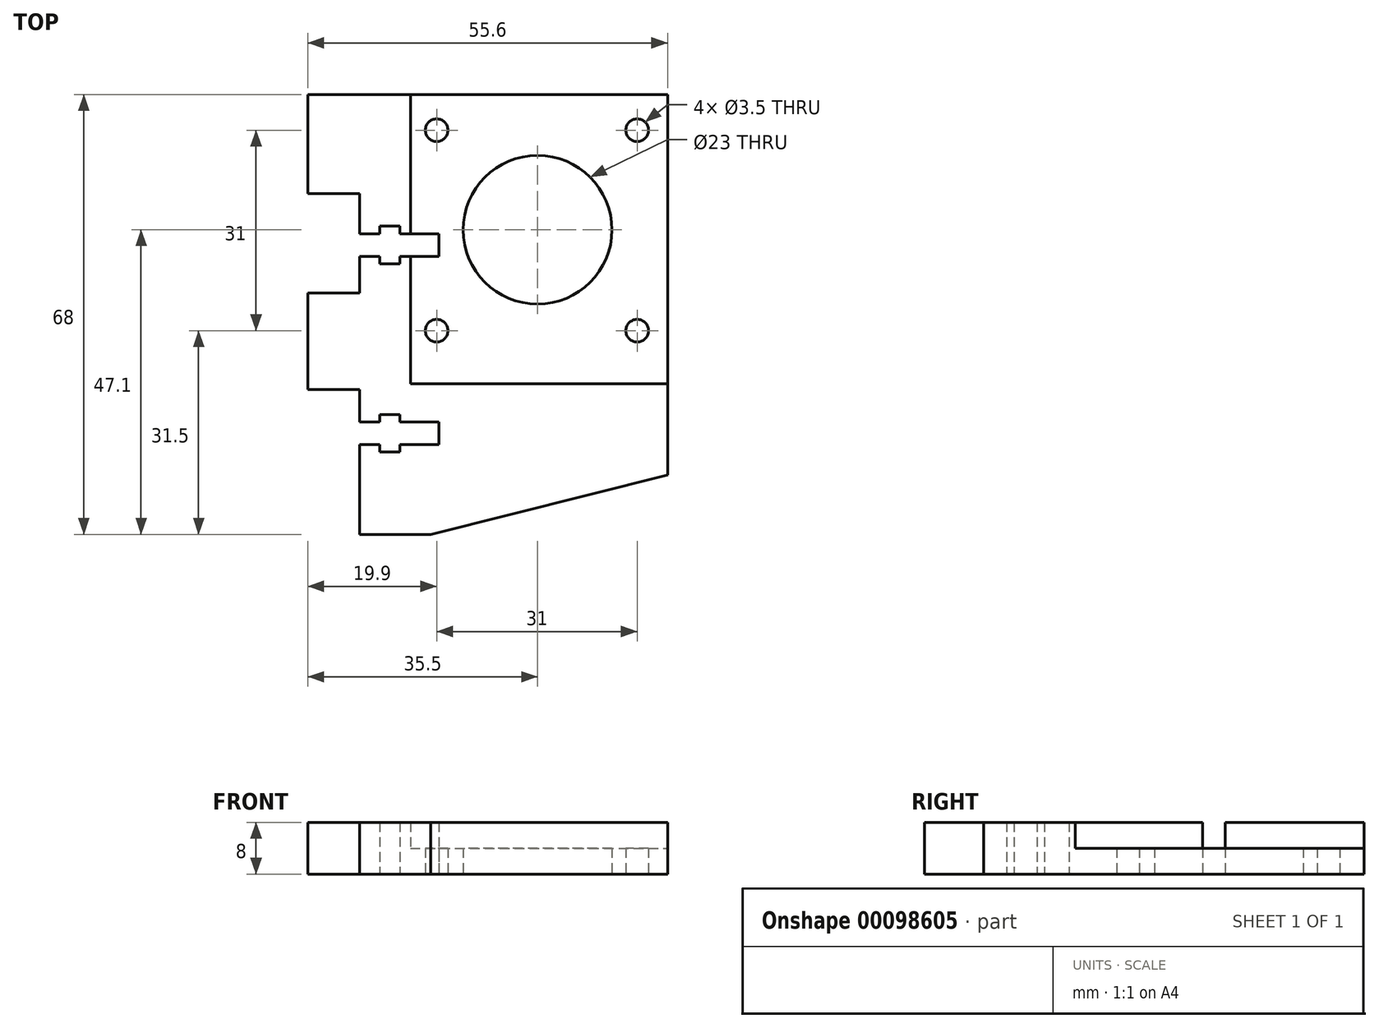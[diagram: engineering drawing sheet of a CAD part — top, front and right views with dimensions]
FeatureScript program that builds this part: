
annotation { "Feature Type Name" : "Feature", "Feature Type Description" : "" }
export const myFeature = defineFeature(function(context is Context, id is Id, definition is map)
    precondition{}
    {
        {
            var Q0;
            Q0=qCreatedBy(makeId("Top.planeOp"),FACE);
            var sketch = newSketch(context, id + "F0", { "sketchPlane" : qUnion([Q0])});
            skCircle(sketch, "E0", {"center": v(0, 0) * mm, "radius": 11.5 * mm});
            skLineSegment(sketch, "E1", {"start": v(0, 11.5) * mm, "end": v(0, 20.9) * mm, "construction": true});
            skLineSegment(sketch, "E2", {"start": v(11.5, 0) * mm, "end": v(20.1, 0) * mm, "construction": true});
            skLineSegment(sketch, "E3", {"start": v(0, 20.9) * mm, "end": v(58.5, 20.9) * mm, "construction": true});
            skLineSegment(sketch, "E4", {"start": v(20.1, 0) * mm, "end": v(20.1, 20.9) * mm});
            skLineSegment(sketch, "E5", {"start": v(-11.5, 0) * mm, "end": v(-27.86, 0) * mm, "construction": true});
            skLineSegment(sketch, "E6", {"start": v(20.1, 0) * mm, "end": v(20.1, -40.2) * mm, "construction": true});
            skLineSegment(sketch, "E7", {"start": v(20.1, -37.9) * mm, "end": v(-35.5, -37.9) * mm, "construction": true});
            skLineSegment(sketch, "E8", {"start": v(0, 20.9) * mm, "end": v(-51.46, 20.9) * mm, "construction": true});
            skLineSegment(sketch, "E9", {"start": v(-35.5, 20.9) * mm, "end": v(-35.5, 5.6) * mm});
            skLineSegment(sketch, "E10", {"start": v(-27.5, -47.1) * mm, "end": v(-16.5, -47.1) * mm});
            skLineSegment(sketch, "E11", {"start": v(20.1, 20.9) * mm, "end": v(20.1, -37.9) * mm});
            skLineSegment(sketch, "E12", {"start": v(-16.5, -47.1) * mm, "end": v(20.1, -37.9) * mm});
            skLineSegment(sketch, "E13.0", {"start": v(-27.5, 5.6) * mm, "end": v(-27.5, -0.6) * mm});
            skLineSegment(sketch, "E14", {"start": v(-32.15, -47.1) * mm, "end": v(-32.15, -24.7) * mm, "construction": true});
            skLineSegment(sketch, "E15", {"start": v(-32.15, -24.7) * mm, "end": v(-27.5, -24.7) * mm});
            skLineSegment(sketch, "E16", {"start": v(-27.5, -24.7) * mm, "end": v(-35.5, -24.7) * mm});
            skLineSegment(sketch, "E17", {"start": v(-32.15, -24.7) * mm, "end": v(-32.15, -9.8) * mm, "construction": true});
            skLineSegment(sketch, "E18", {"start": v(-27.5, -9.8) * mm, "end": v(-35.5, -9.8) * mm});
            skLineSegment(sketch, "E19", {"start": v(-32.15, -9.8) * mm, "end": v(-32.15, 5.6) * mm, "construction": true});
            skLineSegment(sketch, "E20", {"start": v(-32.15, 5.6) * mm, "end": v(-27.5, 5.6) * mm});
            skLineSegment(sketch, "E21", {"start": v(-27.5, 5.6) * mm, "end": v(-35.5, 5.6) * mm});
            skLineSegment(sketch, "E22.trimOffspring", {"start": v(-35.5, -9.8) * mm, "end": v(-35.5, -24.7) * mm});
            skLineSegment(sketch, "E23", {"start": v(-35.5, 20.9) * mm, "end": v(20.1, 20.9) * mm});
            skLineSegment(sketch, "E24.trimOffspring", {"start": v(-27.5, -24.7) * mm, "end": v(-27.5, -29.7) * mm});
            skLineSegment(sketch, "E25.0", {"start": v(-35.5, 15.4) * mm, "end": v(20.1, 15.4) * mm, "construction": true});
            skLineSegment(sketch, "E26.0", {"start": v(15.4, 20.9) * mm, "end": v(15.4, -37.9) * mm, "construction": true});
            skCircle(sketch, "E27", {"center": v(15.4, 15.4) * mm, "radius": 1.75 * mm});
            skLineSegment(sketch, "E28", {"start": v(15.4, 15.4) * mm, "end": v(-15.6, 15.4) * mm, "construction": true});
            skCircle(sketch, "E29", {"center": v(-15.6, 15.4) * mm, "radius": 1.75 * mm});
            skLineSegment(sketch, "E30", {"start": v(-15.6, 15.4) * mm, "end": v(-15.6, -15.6) * mm, "construction": true});
            skCircle(sketch, "E31", {"center": v(-15.6, -15.6) * mm, "radius": 1.75 * mm});
            skLineSegment(sketch, "E32", {"start": v(-15.6, -15.6) * mm, "end": v(15.4, -15.6) * mm, "construction": true});
            skCircle(sketch, "E33", {"center": v(15.4, -15.6) * mm, "radius": 1.75 * mm});
            skLineSegment(sketch, "E34", {"start": v(-24.4, 20.9) * mm, "end": v(-24.4, -0.6) * mm, "construction": true});
            skLineSegment(sketch, "E35.bottom", {"start": v(-27.5, -0.6) * mm, "end": v(-24.39, -0.6) * mm});
            skLineSegment(sketch, "E35.top", {"start": v(-27.5, -4.1) * mm, "end": v(-24.39, -4.1) * mm});
            skLineSegment(sketch, "E35.right", {"start": v(-15.26, -0.6) * mm, "end": v(-15.26, -4.1) * mm});
            skLineSegment(sketch, "E36.trimOffspring", {"start": v(-27.5, -4.1) * mm, "end": v(-27.5, -9.8) * mm});
            skLineSegment(sketch, "E37", {"start": v(-24.39, -4.1) * mm, "end": v(-24.39, -29.7) * mm, "construction": true});
            skLineSegment(sketch, "E38.bottom", {"start": v(-27.5, -29.7) * mm, "end": v(-24.39, -29.7) * mm});
            skLineSegment(sketch, "E38.top", {"start": v(-27.5, -33.2) * mm, "end": v(-24.39, -33.2) * mm});
            skLineSegment(sketch, "E38.right", {"start": v(-15.26, -29.7) * mm, "end": v(-15.26, -33.2) * mm});
            skLineSegment(sketch, "E39.trimOffspring", {"start": v(-27.5, -33.2) * mm, "end": v(-27.5, -47.1) * mm});
            skLineSegment(sketch, "E40.0", {"start": v(-23.1, 5.6) * mm, "end": v(-23.1, -0.6) * mm, "construction": true});
            skLineSegment(sketch, "E41.bottom", {"start": v(-24.4, -0.6) * mm, "end": v(-23.1, -0.6) * mm, "construction": true});
            skLineSegment(sketch, "E41.top", {"start": v(-24.4, -4.1) * mm, "end": v(-21.3, -4.1) * mm, "construction": true});
            skLineSegment(sketch, "E41.left", {"start": v(-24.4, -0.6) * mm, "end": v(-24.4, -4.1) * mm, "construction": true});
            skLineSegment(sketch, "E41.right", {"start": v(-21.3, -0.6) * mm, "end": v(-21.3, -4.1) * mm, "construction": true});
            skLineSegment(sketch, "E42.0", {"start": v(-27.5, -5.25) * mm, "end": v(-15.26, -5.25) * mm, "construction": true});
            skLineSegment(sketch, "E43.bottom", {"start": v(-24.39, -5.25) * mm, "end": v(-21.29, -5.25) * mm, "construction": true});
            skLineSegment(sketch, "E43.top", {"start": v(-24.39, 0.55) * mm, "end": v(-21.29, 0.55) * mm, "construction": true});
            skLineSegment(sketch, "E43.left", {"start": v(-24.39, -5.25) * mm, "end": v(-24.39, 0.55) * mm, "construction": true});
            skLineSegment(sketch, "E43.right", {"start": v(-21.29, -5.25) * mm, "end": v(-21.29, 0.55) * mm, "construction": true});
            skLineSegment(sketch, "E44.bottom", {"start": v(-24.39, 0.55) * mm, "end": v(-21.29, 0.55) * mm});
            skLineSegment(sketch, "E44.top", {"start": v(-24.39, -5.25) * mm, "end": v(-21.29, -5.25) * mm});
            skLineSegment(sketch, "E44.left", {"start": v(-24.39, 0.55) * mm, "end": v(-24.39, -0.6) * mm});
            skLineSegment(sketch, "E44.right", {"start": v(-21.29, 0.55) * mm, "end": v(-21.29, -0.6) * mm});
            skLineSegment(sketch, "E45.trimOffspring", {"start": v(-21.3, -0.6) * mm, "end": v(-15.26, -0.6) * mm});
            skLineSegment(sketch, "E46.trimOffspring", {"start": v(-24.39, -4.1) * mm, "end": v(-24.39, -5.25) * mm});
            skLineSegment(sketch, "E47.trimOffspring", {"start": v(-21.29, -4.1) * mm, "end": v(-21.29, -5.25) * mm});
            skLineSegment(sketch, "E48.trimOffspring", {"start": v(-21.3, -4.1) * mm, "end": v(-15.26, -4.1) * mm});
            skLineSegment(sketch, "E49.0", {"start": v(-27.5, -34.35) * mm, "end": v(-15.26, -34.35) * mm, "construction": true});
            skLineSegment(sketch, "E50.bottom", {"start": v(-24.39, -34.35) * mm, "end": v(-21.29, -34.35) * mm, "construction": true});
            skLineSegment(sketch, "E50.top", {"start": v(-24.39, -28.55) * mm, "end": v(-21.29, -28.55) * mm, "construction": true});
            skLineSegment(sketch, "E50.left", {"start": v(-24.39, -34.35) * mm, "end": v(-24.39, -28.55) * mm, "construction": true});
            skLineSegment(sketch, "E50.right", {"start": v(-21.29, -34.35) * mm, "end": v(-21.29, -28.55) * mm, "construction": true});
            skLineSegment(sketch, "E51.bottom", {"start": v(-24.39, -28.55) * mm, "end": v(-21.29, -28.55) * mm});
            skLineSegment(sketch, "E51.top", {"start": v(-24.39, -34.35) * mm, "end": v(-21.29, -34.35) * mm});
            skLineSegment(sketch, "E51.left", {"start": v(-24.39, -28.55) * mm, "end": v(-24.39, -29.7) * mm});
            skLineSegment(sketch, "E51.right", {"start": v(-21.29, -28.55) * mm, "end": v(-21.29, -29.7) * mm});
            skLineSegment(sketch, "E52.trimOffspring", {"start": v(-21.29, -29.7) * mm, "end": v(-15.26, -29.7) * mm});
            skLineSegment(sketch, "E53.trimOffspring", {"start": v(-21.29, -33.2) * mm, "end": v(-15.26, -33.2) * mm});
            skLineSegment(sketch, "E54.trimOffspring", {"start": v(-21.29, -33.2) * mm, "end": v(-21.29, -34.35) * mm});
            skLineSegment(sketch, "E55.trimOffspring", {"start": v(-24.39, -33.2) * mm, "end": v(-24.39, -34.35) * mm});
            skSolve(sketch);
        }
        {
            var Q0;
            Q0=makeQuery(id+"F0.imprint","IMPRINT",FACE,{"disambiguationData":[TD([[makeQuery(id+"F0.imprint","IMPRINT",EDGE,{"derivedFrom":sQuery(id+"F0.wireOp",EDGE,"E0")}),-1.0]])]});
            extrude(context, id + "F1", {"entities" : qUnion([Q0]), "depth" : 4 * mm});
        }
        {
            var Q0;
            Q0=makeQuery(id+"F1.opExtrude","CAP_FACE",FACE,{"disambiguationData":[OSD([sQuery(id+"F0.wireOp",EDGE,"E0"),sQuery(id+"F0.wireOp",EDGE,"E9"),sQuery(id+"F0.wireOp",EDGE,"E10"),sQuery(id+"F0.wireOp",EDGE,"E11"),sQuery(id+"F0.wireOp",EDGE,"E12"),sQuery(id+"F0.wireOp",EDGE,"E13.0"),sQuery(id+"F0.wireOp",EDGE,"E16"),sQuery(id+"F0.wireOp",EDGE,"E18"),sQuery(id+"F0.wireOp",EDGE,"E21"),sQuery(id+"F0.wireOp",EDGE,"E22.trimOffspring"),sQuery(id+"F0.wireOp",EDGE,"E23"),sQuery(id+"F0.wireOp",EDGE,"E24.trimOffspring"),sQuery(id+"F0.wireOp",EDGE,"E27"),sQuery(id+"F0.wireOp",EDGE,"E29"),sQuery(id+"F0.wireOp",EDGE,"E31"),sQuery(id+"F0.wireOp",EDGE,"E33"),sQuery(id+"F0.wireOp",EDGE,"E35.bottom"),sQuery(id+"F0.wireOp",EDGE,"E35.top"),sQuery(id+"F0.wireOp",EDGE,"E35.right"),sQuery(id+"F0.wireOp",EDGE,"E36.trimOffspring"),sQuery(id+"F0.wireOp",EDGE,"E38.bottom"),sQuery(id+"F0.wireOp",EDGE,"E38.top"),sQuery(id+"F0.wireOp",EDGE,"E38.right"),sQuery(id+"F0.wireOp",EDGE,"E39.trimOffspring"),sQuery(id+"F0.wireOp",EDGE,"E44.bottom"),sQuery(id+"F0.wireOp",EDGE,"E44.top"),sQuery(id+"F0.wireOp",EDGE,"E44.left"),sQuery(id+"F0.wireOp",EDGE,"E44.right"),sQuery(id+"F0.wireOp",EDGE,"E45.trimOffspring"),sQuery(id+"F0.wireOp",EDGE,"E46.trimOffspring"),sQuery(id+"F0.wireOp",EDGE,"E47.trimOffspring"),sQuery(id+"F0.wireOp",EDGE,"E48.trimOffspring"),sQuery(id+"F0.wireOp",EDGE,"E51.bottom"),sQuery(id+"F0.wireOp",EDGE,"E51.top"),sQuery(id+"F0.wireOp",EDGE,"E51.left"),sQuery(id+"F0.wireOp",EDGE,"E51.right"),sQuery(id+"F0.wireOp",EDGE,"E52.trimOffspring"),sQuery(id+"F0.wireOp",EDGE,"E53.trimOffspring"),sQuery(id+"F0.wireOp",EDGE,"E54.trimOffspring"),sQuery(id+"F0.wireOp",EDGE,"E55.trimOffspring")])],"isStart":false});
            var sketch = newSketch(context, id + "F2", { "sketchPlane" : qUnion([Q0])});
            skLineSegment(sketch, "E56.0.0", {"start": v(-19.65, 20.9) * mm, "end": v(-35.5, 20.9) * mm});
            skLineSegment(sketch, "E56.0.1", {"start": v(-35.5, 20.9) * mm, "end": v(-35.5, 5.6) * mm});
            skLineSegment(sketch, "E56.0.2", {"start": v(-35.5, 5.6) * mm, "end": v(-27.5, 5.6) * mm});
            skLineSegment(sketch, "E56.0.3", {"start": v(-27.5, 5.6) * mm, "end": v(-27.5, -0.6) * mm});
            skLineSegment(sketch, "E56.0.4", {"start": v(-27.5, -0.6) * mm, "end": v(-24.39, -0.6) * mm});
            skLineSegment(sketch, "E56.0.5", {"start": v(-24.39, -0.6) * mm, "end": v(-24.39, 0.55) * mm});
            skLineSegment(sketch, "E56.0.6", {"start": v(-24.39, 0.55) * mm, "end": v(-21.29, 0.55) * mm});
            skLineSegment(sketch, "E56.0.7", {"start": v(-21.29, 0.55) * mm, "end": v(-21.29, -0.6) * mm});
            skLineSegment(sketch, "E56.0.8", {"start": v(-21.29, -0.6) * mm, "end": v(-19.65, -0.6) * mm});
            skLineSegment(sketch, "E56.0.9", {"start": v(-15.26, -0.6) * mm, "end": v(-15.26, -4.1) * mm});
            skLineSegment(sketch, "E56.0.10", {"start": v(-19.65, -4.1) * mm, "end": v(-21.29, -4.1) * mm});
            skLineSegment(sketch, "E56.0.11", {"start": v(-21.29, -4.1) * mm, "end": v(-21.29, -5.25) * mm});
            skLineSegment(sketch, "E56.0.12", {"start": v(-21.29, -5.25) * mm, "end": v(-24.39, -5.25) * mm});
            skLineSegment(sketch, "E56.0.13", {"start": v(-24.39, -5.25) * mm, "end": v(-24.39, -4.1) * mm});
            skLineSegment(sketch, "E56.0.14", {"start": v(-24.39, -4.1) * mm, "end": v(-27.5, -4.1) * mm});
            skLineSegment(sketch, "E56.0.15", {"start": v(-27.5, -4.1) * mm, "end": v(-27.5, -9.8) * mm});
            skLineSegment(sketch, "E56.0.16", {"start": v(-27.5, -9.8) * mm, "end": v(-35.5, -9.8) * mm});
            skLineSegment(sketch, "E56.0.17", {"start": v(-35.5, -9.8) * mm, "end": v(-35.5, -24.7) * mm});
            skLineSegment(sketch, "E56.0.18", {"start": v(-35.5, -24.7) * mm, "end": v(-27.5, -24.7) * mm});
            skLineSegment(sketch, "E56.0.19", {"start": v(-27.5, -24.7) * mm, "end": v(-27.5, -29.7) * mm});
            skLineSegment(sketch, "E56.0.20", {"start": v(-27.5, -29.7) * mm, "end": v(-24.39, -29.7) * mm});
            skLineSegment(sketch, "E56.0.21", {"start": v(-24.39, -29.7) * mm, "end": v(-24.39, -28.55) * mm});
            skLineSegment(sketch, "E56.0.22", {"start": v(-24.39, -28.55) * mm, "end": v(-21.29, -28.55) * mm});
            skLineSegment(sketch, "E56.0.23", {"start": v(-21.29, -28.55) * mm, "end": v(-21.29, -29.7) * mm});
            skLineSegment(sketch, "E56.0.24", {"start": v(-21.29, -29.7) * mm, "end": v(-19.65, -29.7) * mm});
            skLineSegment(sketch, "E56.0.25", {"start": v(-15.26, -29.7) * mm, "end": v(-15.26, -33.2) * mm});
            skLineSegment(sketch, "E56.0.26", {"start": v(-19.65, -33.2) * mm, "end": v(-21.29, -33.2) * mm});
            skLineSegment(sketch, "E56.0.27", {"start": v(-21.29, -33.2) * mm, "end": v(-21.29, -34.35) * mm});
            skLineSegment(sketch, "E56.0.28", {"start": v(-21.29, -34.35) * mm, "end": v(-24.39, -34.35) * mm});
            skLineSegment(sketch, "E56.0.29", {"start": v(-24.39, -34.35) * mm, "end": v(-24.39, -33.2) * mm});
            skLineSegment(sketch, "E56.0.30", {"start": v(-24.39, -33.2) * mm, "end": v(-27.5, -33.2) * mm});
            skLineSegment(sketch, "E56.0.31", {"start": v(-27.5, -33.2) * mm, "end": v(-27.5, -47.1) * mm});
            skLineSegment(sketch, "E56.0.32", {"start": v(-27.5, -47.1) * mm, "end": v(-19.65, -47.1) * mm});
            skLineSegment(sketch, "E57", {"start": v(-17.35, 15.33) * mm, "end": v(-19.65, 15.33) * mm, "construction": true});
            skLineSegment(sketch, "E58", {"start": v(-19.65, 15.33) * mm, "end": v(-19.65, -47.1) * mm});
            skLineSegment(sketch, "E59", {"start": v(-19.65, -47.1) * mm, "end": v(-19.65, 20.9) * mm});
            skPoint(sketch, "E56.0.33.start.orphan", {"position": v(-16.5, -47.1) * mm});
            skPoint(sketch, "E56.0.34.end.orphan", {"position": v(20.1, 20.9) * mm});
            skPoint(sketch, "E56.0.34.start.orphan", {"position": v(20.1, -37.9) * mm});
            skLineSegment(sketch, "E60", {"start": v(-19.65, -23.78) * mm, "end": v(20.1, -23.78) * mm});
            skSolve(sketch);
        }
        {
            var Q0;
            {var subQ3=sQuery(id+"F2.wireOp",EDGE,"E56.0.0");Q0=makeQuery(id+"F2.imprint","IMPRINT",FACE,{"disambiguationData":[TD([[makeQuery(id+"F2.imprint","IMPRINT",EDGE,{"derivedFrom":subQ3}),-1.0]])]});}
            var Q1;
            {var subQ0=sQuery(id+"F2.wireOp",EDGE,"E56.0.10");Q1=makeQuery(id+"F2.imprint","IMPRINT",FACE,{"disambiguationData":[TD([[makeQuery(id+"F2.imprint","IMPRINT",EDGE,{"derivedFrom":subQ0}),-1.0]])]});}
            var Q2;
            {var subQ0=sQuery(id+"F2.wireOp",EDGE,"E56.0.26");Q2=makeQuery(id+"F2.imprint","IMPRINT",FACE,{"disambiguationData":[TD([[makeQuery(id+"F2.imprint","IMPRINT",EDGE,{"derivedFrom":subQ0}),-1.0]])]});}
            var Q3;
            {var subQ10=sQuery(id+"F2.wireOp",EDGE,"E56.0.25");Q3=makeQuery(id+"F2.imprint","IMPRINT",FACE,{"disambiguationData":[TD([[makeQuery(id+"F2.imprint","IMPRINT",EDGE,{"derivedFrom":subQ10}),1.0]])]});}
            extrude(context, id + "F3", {"entities" : qUnion([Q0, Q1, Q2, Q3]), "operationType" : NewBodyOperationType.ADD, "depth" : 4 * mm});
        }
    });
